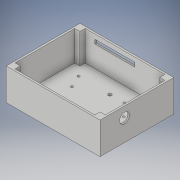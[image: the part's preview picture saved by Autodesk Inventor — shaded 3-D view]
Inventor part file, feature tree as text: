
AUTODESK INVENTOR PART (.ipt)
format: ipt  version: 2018 (Build 220112000, 112)  size: 172,544 bytes
history: native  units: in
note: dims shown in document units (in); Inventor stores cm internally (conversion verified against a paired STEP export)
features: extrude x6, sketch x6
ambient origin geometry x8: Origin, YZ Plane, XZ Plane, XY Plane, X Axis, Y Axis, Z Axis, Center Point
bodies: Solid1 (feature_tree)
feature tree (12):
  extrude  "Extrusion1"  Depth=3.701in
  extrude  "Extrusion2"  Depth=4.527in
  extrude  "Extrusion3"  Depth=0.354in
  extrude  "Extrusion4"  Depth=0.354in
  extrude  "Extrusion5"  Depth=1.5in TaperAngle=0.0deg
  extrude  "Extrusion6"  Depth=2.0in
  sketch  "Sketch1"  dims[d0=4.705in d1=3.701in]
  sketch  "Sketch2"  dims[d2=0.089in d3=0.0in d4=4.527in]
  sketch  "Sketch3"  dims[d5=3.523in d6=0.354in]
  sketch  "Sketch4"  dims[d7=0.354in d10=0.354in]
  sketch  "Sketch6"  dims[d11=0.354in d14=1.5in d15=0.0in]
  sketch  "Sketch7"  dims[d18=0.164in d19=0.164in d20=0.0in d21=0.0in d22=3.42in d23=2.271in d25=0.787in d30=0.112in d31=0.112in d36=0.112in d37=0.112in d38=0.118in d39=0.118in d40=0.118in d41=0.118in d42=0.0in d43=0.0in d44=0.5in d45=1.5in d46=0.0in d47=2.0in d48=1.0in d49=0.0in]
